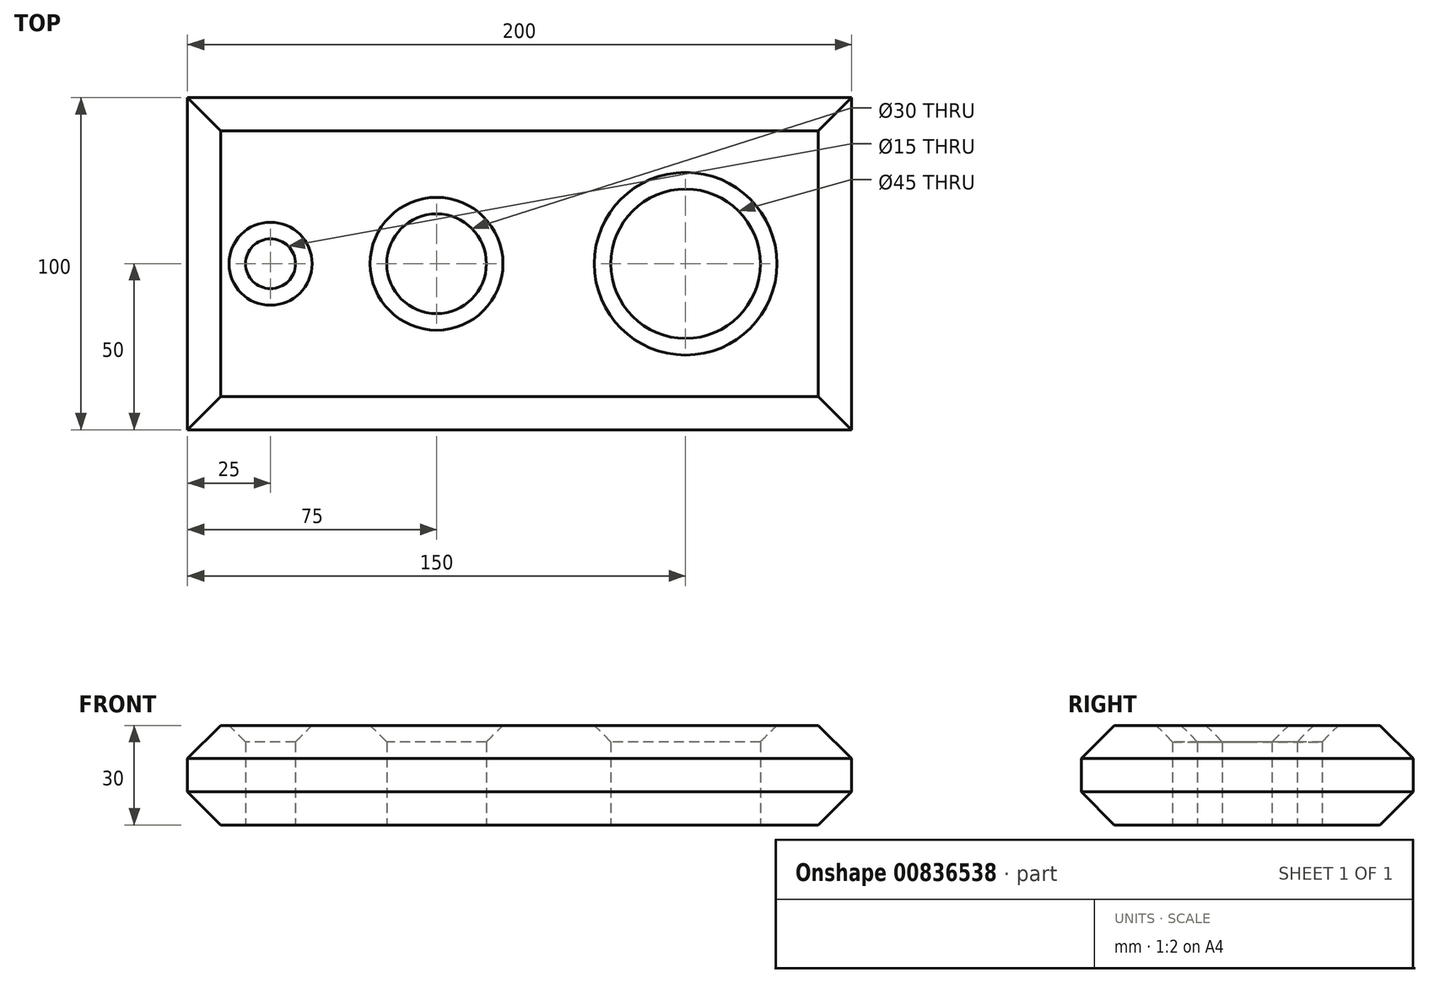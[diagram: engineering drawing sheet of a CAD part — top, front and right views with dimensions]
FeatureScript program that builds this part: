
annotation { "Feature Type Name" : "Feature", "Feature Type Description" : "" }
export const myFeature = defineFeature(function(context is Context, id is Id, definition is map)
    precondition{}
    {
        {
            var Q0;
            Q0=qCreatedBy(makeId("Top.planeOp"),FACE);
            var sketch = newSketch(context, id + "F0", { "sketchPlane" : qUnion([Q0])});
            skLineSegment(sketch, "E0.bottom", {"start": v(-100, -50) * mm, "end": v(100, -50) * mm});
            skLineSegment(sketch, "E0.top", {"start": v(-100, 50) * mm, "end": v(100, 50) * mm});
            skLineSegment(sketch, "E0.left", {"start": v(-100, -50) * mm, "end": v(-100, 50) * mm});
            skLineSegment(sketch, "E0.right", {"start": v(100, -50) * mm, "end": v(100, 50) * mm});
            skCircle(sketch, "E1", {"center": v(-75, 0) * mm, "radius": 7.5 * mm});
            skPoint(sketch, "E1.centerSnap0", {"position": v(-100, 0) * mm});
            skCircle(sketch, "E2", {"center": v(-25, 0) * mm, "radius": 15 * mm});
            skCircle(sketch, "E3", {"center": v(50, 0) * mm, "radius": 22.5 * mm});
            skSolve(sketch);
        }
        {
            var Q0;
            Q0=makeQuery(id+"F0.imprint","IMPRINT",FACE,{"disambiguationData":[TD([[makeQuery(id+"F0.imprint","IMPRINT",EDGE,{"derivedFrom":sQuery(id+"F0.wireOp",EDGE,"E0.bottom")}),1.0]])]});
            extrude(context, id + "F1", {"entities" : qUnion([Q0]), "depth" : 30 * mm, "offsetDistance" : 25 * mm});
        }
        {
            var Q0;
            Q0=makeQuery(id+"F1.opExtrude","CAP_EDGE",EDGE,{"disambiguationData":[OSD([sQuery(id+"F0.wireOp",EDGE,"E1")])],"isStart":false});
            var Q1;
            Q1=makeQuery(id+"F1.opExtrude","CAP_EDGE",EDGE,{"disambiguationData":[OSD([sQuery(id+"F0.wireOp",EDGE,"E2")])],"isStart":false});
            var Q2;
            Q2=makeQuery(id+"F1.opExtrude","CAP_EDGE",EDGE,{"disambiguationData":[OSD([sQuery(id+"F0.wireOp",EDGE,"E3")])],"isStart":false});
            chamfer(context, id + "F2", {"entities" : qUnion([Q0, Q1, Q2]), "width" : 5 * mm, "tangentPropagation" : true});
        }
        {
            var Q0;
            Q0=makeQuery(id+"F1.opExtrude","CAP_EDGE",EDGE,{"disambiguationData":[OSD([sQuery(id+"F0.wireOp",EDGE,"E0.right")])],"isStart":false});
            var Q1;
            Q1=makeQuery(id+"F1.opExtrude","CAP_EDGE",EDGE,{"disambiguationData":[OSD([sQuery(id+"F0.wireOp",EDGE,"E0.right")])],"isStart":true});
            var Q2;
            Q2=makeQuery(id+"F1.opExtrude","CAP_EDGE",EDGE,{"disambiguationData":[OSD([sQuery(id+"F0.wireOp",EDGE,"E0.left")])],"isStart":false});
            var Q3;
            Q3=makeQuery(id+"F1.opExtrude","CAP_EDGE",EDGE,{"disambiguationData":[OSD([sQuery(id+"F0.wireOp",EDGE,"E0.left")])],"isStart":true});
            chamfer(context, id + "F3", {"entities" : qUnion([Q0, Q1, Q2, Q3]), "width" : 10 * mm, "tangentPropagation" : true});
        }
        {
            var Q0;
            Q0=makeQuery(id+"F1.opExtrude","CAP_EDGE",EDGE,{"disambiguationData":[OSD([sQuery(id+"F0.wireOp",EDGE,"E0.bottom")])],"isStart":false});
            var Q1;
            Q1=makeQuery(id+"F1.opExtrude","CAP_EDGE",EDGE,{"disambiguationData":[OSD([sQuery(id+"F0.wireOp",EDGE,"E0.top")])],"isStart":false});
            var Q2;
            Q2=makeQuery(id+"F1.opExtrude","CAP_EDGE",EDGE,{"disambiguationData":[OSD([sQuery(id+"F0.wireOp",EDGE,"E0.top")])],"isStart":true});
            var Q3;
            Q3=makeQuery(id+"F1.opExtrude","CAP_EDGE",EDGE,{"disambiguationData":[OSD([sQuery(id+"F0.wireOp",EDGE,"E0.bottom")])],"isStart":true});
            chamfer(context, id + "F4", {"entities" : qUnion([Q0, Q1, Q2, Q3]), "width" : 10 * mm, "tangentPropagation" : true});
        }
    });
